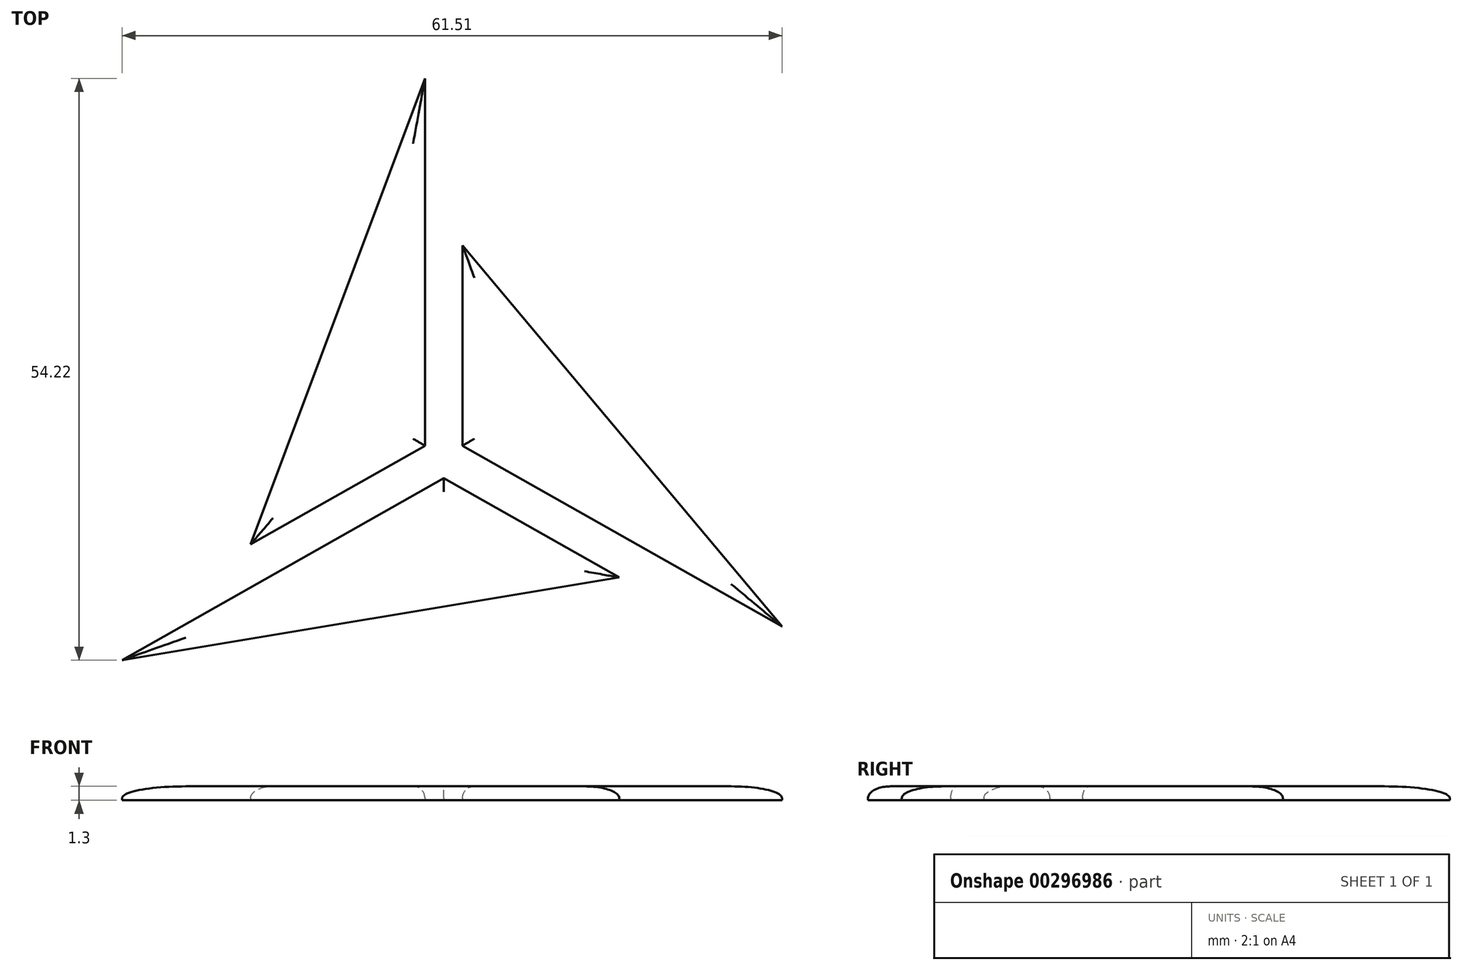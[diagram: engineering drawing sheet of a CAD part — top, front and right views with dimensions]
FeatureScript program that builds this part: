
annotation { "Feature Type Name" : "Feature", "Feature Type Description" : "" }
export const myFeature = defineFeature(function(context is Context, id is Id, definition is map)
    precondition{}
    {
        {
            var Q0;
            Q0=qCreatedBy(makeId("Top.planeOp"),FACE);
            var sketch = newSketch(context, id + "F0", { "sketchPlane" : qUnion([Q0])});
            skLineSegment(sketch, "E0.0", {"start": v(-40.27, 11.94) * mm, "end": v(-24.02, 55.35) * mm});
            skLineSegment(sketch, "E0.1", {"start": v(-24.02, 21.13) * mm, "end": v(-40.27, 11.94) * mm});
            skLineSegment(sketch, "E0.2", {"start": v(-24.02, 55.35) * mm, "end": v(-24.02, 21.13) * mm});
            skLineSegment(sketch, "E1.0", {"start": v(-20.52, 39.8) * mm, "end": v(9.26, 4.28) * mm});
            skLineSegment(sketch, "E1.1", {"start": v(-20.52, 21.13) * mm, "end": v(-20.52, 39.8) * mm});
            skLineSegment(sketch, "E1.2", {"start": v(9.26, 4.28) * mm, "end": v(-20.52, 21.13) * mm});
            skLineSegment(sketch, "E2.0", {"start": v(-5.92, 8.85) * mm, "end": v(-52.25, 1.13) * mm});
            skLineSegment(sketch, "E2.1", {"start": v(-22.27, 18.1) * mm, "end": v(-5.92, 8.85) * mm});
            skLineSegment(sketch, "E2.2", {"start": v(-52.25, 1.13) * mm, "end": v(-22.27, 18.1) * mm});
            skSolve(sketch);
        }
        {
            var Q0;
            Q0 = qSketchRegion(id + "F0", true);
            extrude(context, id + "F1", {"entities" : qUnion([Q0]), "depth" : 1.3 * mm, "offsetDistance" : 25 * mm});
        }
        {
            var Q0;
            Q0=makeQuery(id+"F1.opExtrude","CAP_FACE",FACE,{"disambiguationData":[OSD([sQuery(id+"F0.wireOp",EDGE,"E0.0"),sQuery(id+"F0.wireOp",EDGE,"E0.1"),sQuery(id+"F0.wireOp",EDGE,"E0.2")])],"isStart":false});
            var Q1;
            Q1=makeQuery(id+"F1.opExtrude","CAP_FACE",FACE,{"disambiguationData":[OSD([sQuery(id+"F0.wireOp",EDGE,"E1.0"),sQuery(id+"F0.wireOp",EDGE,"E1.1"),sQuery(id+"F0.wireOp",EDGE,"E1.2")])],"isStart":false});
            var Q2;
            Q2=makeQuery(id+"F1.opExtrude","CAP_FACE",FACE,{"disambiguationData":[OSD([sQuery(id+"F0.wireOp",EDGE,"E2.0"),sQuery(id+"F0.wireOp",EDGE,"E2.1"),sQuery(id+"F0.wireOp",EDGE,"E2.2")])],"isStart":false});
            fillet(context, id + "F2", {"entities" : qUnion([Q0, Q1, Q2]), "radius" : 1.1 * mm, "tangentPropagation" : true, "allowEdgeOverflow" : false});
        }
    });
